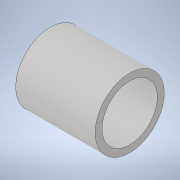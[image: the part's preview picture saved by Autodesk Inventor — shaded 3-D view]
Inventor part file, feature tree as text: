
AUTODESK INVENTOR PART (.ipt)
format: ipt  version: 2021 (Build 250183000, 183)  size: 98,304 bytes
history: native  units: in
note: dims shown in document units (in); Inventor stores cm internally (conversion verified against a paired STEP export)
features: extrude x1, sketch x1
ambient origin geometry x8: Origin, YZ Plane, XZ Plane, XY Plane, X Axis, Y Axis, Z Axis, Center Point
bodies: Solid1 (feature_tree)
feature tree (2):
  extrude  "Extrusion1"  Depth=0.453in
  sketch  "Sketch1"  dims[d0=0.394in d1=0.3153in d2=0.453in d3=0.0in]
